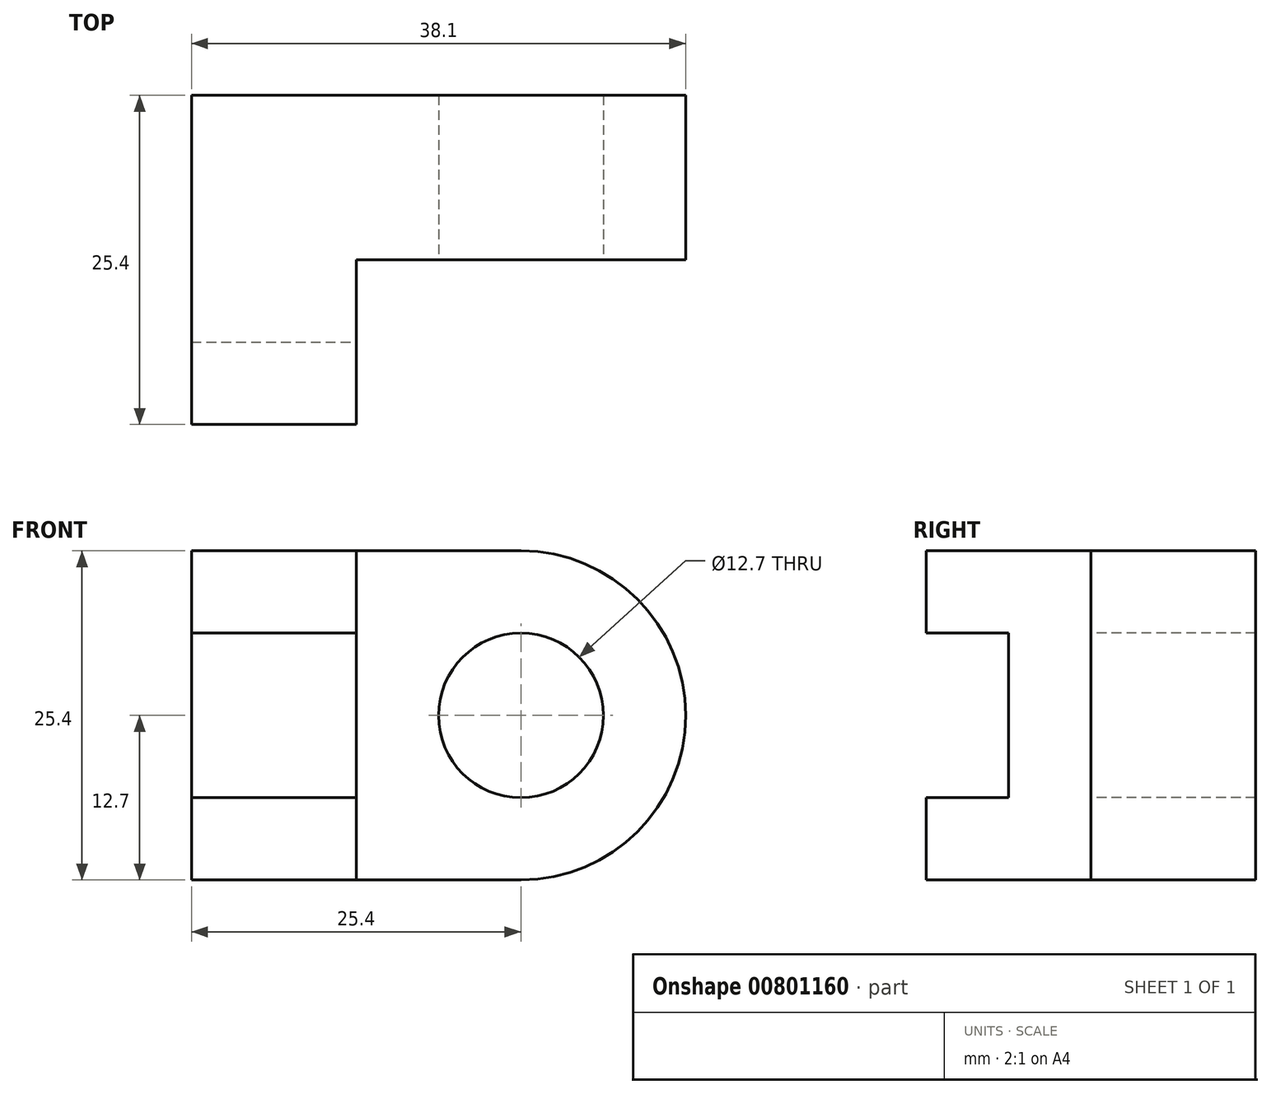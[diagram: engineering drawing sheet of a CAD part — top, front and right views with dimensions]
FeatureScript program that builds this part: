
annotation { "Feature Type Name" : "Feature", "Feature Type Description" : "" }
export const myFeature = defineFeature(function(context is Context, id is Id, definition is map)
    precondition{}
    {
        {
            var Q0;
            Q0=qCreatedBy(makeId("Front.planeOp"),FACE);
            var sketch = newSketch(context, id + "F0", { "sketchPlane" : qUnion([Q0])});
            skLineSegment(sketch, "E0", {"start": v(0, 0) * mm, "end": v(50.8, 0) * mm});
            skLineSegment(sketch, "E1", {"start": v(50.8, 0) * mm, "end": v(50.8, 25.4) * mm});
            skLineSegment(sketch, "E2", {"start": v(50.8, 25.4) * mm, "end": v(0, 25.4) * mm});
            skLineSegment(sketch, "E3", {"start": v(0, 25.4) * mm, "end": v(0, 0) * mm});
            skSolve(sketch);
        }
        {
            var Q0;
            Q0 = qSketchRegion(id + "F0", true);
            extrude(context, id + "F1", {"entities" : qUnion([Q0]), "depth" : 25.4 * mm, "offsetDistance" : 25.4 * mm});
        }
        {
            var Q0;
            Q0=makeQuery(id+"F1.opExtrude","CAP_FACE",FACE,{"disambiguationData":[OSD([sQuery(id+"F0.wireOp",EDGE,"E0"),sQuery(id+"F0.wireOp",EDGE,"E1"),sQuery(id+"F0.wireOp",EDGE,"E2"),sQuery(id+"F0.wireOp",EDGE,"E3")])],"isStart":false});
            var sketch = newSketch(context, id + "F2", { "sketchPlane" : qUnion([Q0])});
            skLineSegment(sketch, "E4", {"start": v(0, 25.4) * mm, "end": v(12.7, 25.4) * mm});
            skLineSegment(sketch, "E5", {"start": v(12.7, 25.4) * mm, "end": v(12.7, 0) * mm});
            skSolve(sketch);
        }
        {
            var Q0;
            {var subQ0=sQuery(id+"F2.wireOp",EDGE,"E5");Q0=makeQuery(id+"F2.imprint","IMPRINT",FACE,{"disambiguationData":[TD([[makeQuery(id+"F2.imprint","IMPRINT",EDGE,{"derivedFrom":subQ0}),1.0]])]});}
            extrude(context, id + "F3", {"entities" : qUnion([Q0]), "operationType" : NewBodyOperationType.REMOVE, "oppositeDirection" : true, "depth" : 12.7 * mm, "offsetDistance" : 25.4 * mm});
        }
        {
            var Q0;
            Q0=makeQuery(id+"F3.boolean.opBoolean","COPY",FACE,{"derivedFrom":makeQuery(id+"F3.opExtrude","CAP_FACE",FACE,{"disambiguationData":[OSD([sQuery(id+"F0.wireOp",EDGE,"E0"),sQuery(id+"F0.wireOp",EDGE,"E1"),sQuery(id+"F0.wireOp",EDGE,"E2"),sQuery(id+"F2.wireOp",EDGE,"E5")])],"isStart":false})});
            var sketch = newSketch(context, id + "F4", { "sketchPlane" : qUnion([Q0])});
            skLineSegment(sketch, "E6", {"start": v(12.7, 25.4) * mm, "end": v(25.4, 25.4) * mm, "construction": true});
            skLineSegment(sketch, "E7", {"start": v(25.4, 25.4) * mm, "end": v(25.4, 0) * mm, "construction": true});
            skCircle(sketch, "E8", {"center": v(25.4, 12.7) * mm, "radius": 6.35 * mm});
            skArc(sketch, "E9", {"start": v(25.4, 0) * mm, "mid": v(38.1, 12.7) * mm, "end": v(25.4, 25.4) * mm});
            skSolve(sketch);
        }
        {
            var Q0;
            Q0 = qSketchRegion(id + "F4", true);
            var Q1;
            {var subQ0=sQuery(id+"F4.wireOp",EDGE,"E9");Q1=makeQuery(id+"F4.imprint","IMPRINT",FACE,{"disambiguationData":[TD([[makeQuery(id+"F4.imprint","IMPRINT",EDGE,{"derivedFrom":subQ0}),-1.0]])]});}
            extrude(context, id + "F5", {"entities" : qUnion([Q0, Q1]), "operationType" : NewBodyOperationType.REMOVE, "oppositeDirection" : true, "depth" : 25.4 * mm, "offsetDistance" : 25.4 * mm});
        }
        {
            var Q0;
            Q0=makeQuery(id+"F3.boolean.opBoolean","COPY",FACE,{"derivedFrom":makeQuery(id+"F3.opExtrude","SWEPT_FACE",FACE,{"disambiguationData":[OSD([sQuery(id+"F2.wireOp",EDGE,"E5")])]})});
            var sketch = newSketch(context, id + "F6", { "sketchPlane" : qUnion([Q0])});
            skLineSegment(sketch, "E10", {"start": v(-25.4, 25.4) * mm, "end": v(-25.4, 19.05) * mm, "construction": true});
            skLineSegment(sketch, "E11", {"start": v(-25.4, 19.05) * mm, "end": v(-19.05, 19.05) * mm});
            skLineSegment(sketch, "E12", {"start": v(-19.05, 19.05) * mm, "end": v(-19.05, 6.35) * mm});
            skPoint(sketch, "E12.endSnap0", {"position": v(-19.05, 0) * mm});
            skLineSegment(sketch, "E13", {"start": v(-19.05, 6.35) * mm, "end": v(-25.4, 6.35) * mm});
            skSolve(sketch);
        }
        {
            var Q0;
            Q0 = qSketchRegion(id + "F6", true);
            var Q1;
            {var subQ0=sQuery(id+"F6.wireOp",EDGE,"E11");Q1=makeQuery(id+"F6.imprint","IMPRINT",FACE,{"disambiguationData":[TD([[makeQuery(id+"F6.imprint","IMPRINT",EDGE,{"derivedFrom":subQ0}),-1.0]])]});}
            extrude(context, id + "F7", {"entities" : qUnion([Q0, Q1]), "operationType" : NewBodyOperationType.REMOVE, "oppositeDirection" : true, "depth" : 25.4 * mm, "offsetDistance" : 25.4 * mm});
        }
    });
